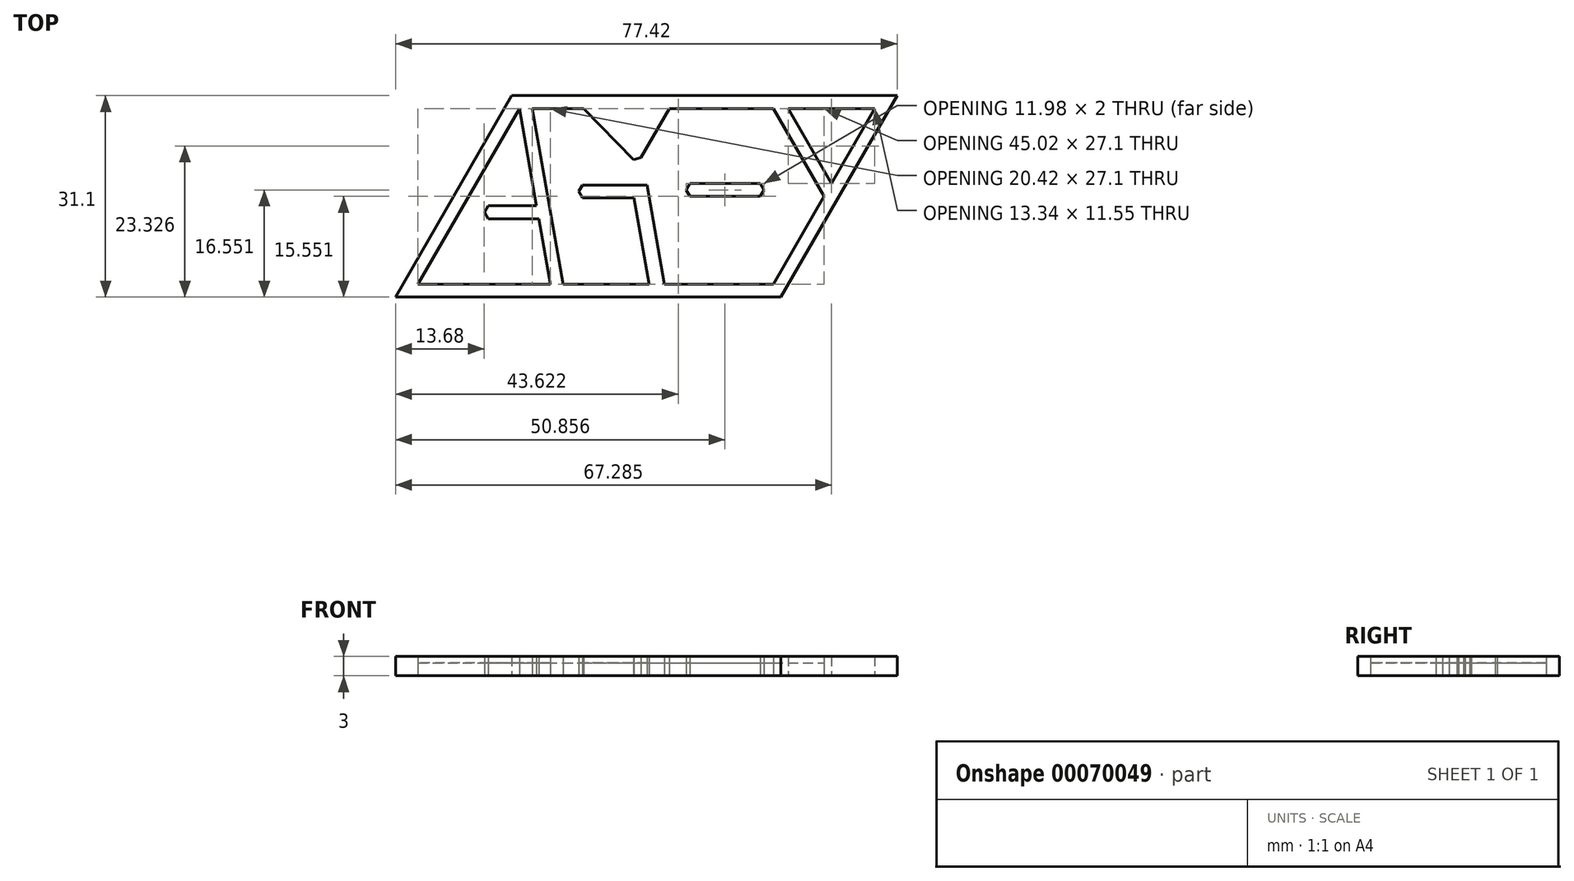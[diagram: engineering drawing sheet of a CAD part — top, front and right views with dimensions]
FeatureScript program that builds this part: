
annotation { "Feature Type Name" : "Feature", "Feature Type Description" : "" }
export const myFeature = defineFeature(function(context is Context, id is Id, definition is map)
    precondition{}
    {
        {
            var Q0;
            Q0=qCreatedBy(makeId("Top.planeOp"),FACE);
            var sketch = newSketch(context, id + "F0", { "sketchPlane" : qUnion([Q0])});
            skLineSegment(sketch, "E0", {"start": v(-33.9, -15.39) * mm, "end": v(-13.47, -15.39) * mm});
            skLineSegment(sketch, "E1", {"start": v(-13.47, -15.39) * mm, "end": v(-18.25, 11.71) * mm});
            skLineSegment(sketch, "E2", {"start": v(-18.25, 11.71) * mm, "end": v(-33.9, -15.39) * mm});
            skLineSegment(sketch, "E3", {"start": v(-15.25, -5.3) * mm, "end": v(-23.05, -5.3) * mm});
            skLineSegment(sketch, "E4", {"start": v(-13.47, -15.39) * mm, "end": v(20.95, -15.39) * mm});
            skLineSegment(sketch, "E5", {"start": v(-18.25, 11.71) * mm, "end": v(20.95, 11.71) * mm});
            skLineSegment(sketch, "E6", {"start": v(20.95, -15.39) * mm, "end": v(28.77, -1.84) * mm});
            skLineSegment(sketch, "E7", {"start": v(28.77, -1.84) * mm, "end": v(20.95, 11.71) * mm});
            skLineSegment(sketch, "E8", {"start": v(18.9, -1.84) * mm, "end": v(8.08, -1.84) * mm});
            skPoint(sketch, "E9.endSnap0", {"position": v(-15.86, -1.84) * mm});
            skLineSegment(sketch, "E10.0", {"start": v(-19.4, 13.71) * mm, "end": v(22.1, 13.71) * mm});
            skLineSegment(sketch, "E10.1", {"start": v(-37.36, -17.39) * mm, "end": v(-13.96, -17.39) * mm});
            skLineSegment(sketch, "E10.2", {"start": v(-13.96, -17.39) * mm, "end": v(22.1, -17.39) * mm});
            skLineSegment(sketch, "E10.3", {"start": v(-19.4, 13.71) * mm, "end": v(-37.36, -17.39) * mm});
            skLineSegment(sketch, "E10.4", {"start": v(22.1, -17.39) * mm, "end": v(31.08, -1.84) * mm});
            skLineSegment(sketch, "E11", {"start": v(-23.05, -3.3) * mm, "end": v(-15.6, -3.3) * mm});
            skLineSegment(sketch, "E12", {"start": v(-16.25, 11.71) * mm, "end": v(-11.47, -15.39) * mm});
            skLineSegment(sketch, "E13", {"start": v(-18.25, 11.71) * mm, "end": v(-16.25, 11.71) * mm});
            skLineSegment(sketch, "E14", {"start": v(1.44, -15.39) * mm, "end": v(-0.56, -15.39) * mm});
            skLineSegment(sketch, "E15", {"start": v(-8.53, -2.08) * mm, "end": v(-0.56, -2.08) * mm});
            skLineSegment(sketch, "E16", {"start": v(8.08, 0.16) * mm, "end": v(18.9, 0.16) * mm});
            skLineSegment(sketch, "E17", {"start": v(1.44, -0.08) * mm, "end": v(-8.53, -0.08) * mm});
            skLineSegment(sketch, "E18", {"start": v(-0.64, 3.83) * mm, "end": v(-8.32, 11.71) * mm});
            skLineSegment(sketch, "E19", {"start": v(-23.05, -5.3) * mm, "end": v(-23.62, -4.3) * mm});
            skLineSegment(sketch, "E20", {"start": v(-23.62, -4.3) * mm, "end": v(-23.05, -3.3) * mm});
            skLineSegment(sketch, "E21", {"start": v(-8.53, -2.08) * mm, "end": v(-9.1, -1.08) * mm});
            skLineSegment(sketch, "E22", {"start": v(-9.1, -1.08) * mm, "end": v(-8.53, -0.08) * mm});
            skLineSegment(sketch, "E23", {"start": v(0.8, 5.23) * mm, "end": v(-5.57, 11.71) * mm});
            skLineSegment(sketch, "E24", {"start": v(-0.64, 3.83) * mm, "end": v(0.48, 4.12) * mm});
            skLineSegment(sketch, "E25", {"start": v(0.48, 4.12) * mm, "end": v(0.8, 5.23) * mm});
            skLineSegment(sketch, "E26", {"start": v(8.08, 0.16) * mm, "end": v(7.5, -0.84) * mm});
            skLineSegment(sketch, "E27", {"start": v(7.5, -0.84) * mm, "end": v(8.08, -1.84) * mm});
            skLineSegment(sketch, "E28", {"start": v(18.9, 0.16) * mm, "end": v(19.49, -0.84) * mm});
            skLineSegment(sketch, "E29", {"start": v(19.49, -0.84) * mm, "end": v(18.9, -1.84) * mm});
            skLineSegment(sketch, "E30", {"start": v(31.08, -1.84) * mm, "end": v(40.06, 13.71) * mm});
            skLineSegment(sketch, "E31", {"start": v(22.1, 13.71) * mm, "end": v(40.06, 13.71) * mm});
            skLineSegment(sketch, "E32", {"start": v(29.93, 0.16) * mm, "end": v(36.6, 11.71) * mm});
            skLineSegment(sketch, "E33", {"start": v(29.93, 0.16) * mm, "end": v(23.26, 11.71) * mm});
            skLineSegment(sketch, "E34", {"start": v(23.26, 11.71) * mm, "end": v(36.6, 11.71) * mm});
            skLineSegment(sketch, "E35", {"start": v(-0.56, -2.08) * mm, "end": v(1.79, -15.39) * mm});
            skLineSegment(sketch, "E36", {"start": v(1.44, -0.08) * mm, "end": v(4.14, -15.39) * mm});
            skLineSegment(sketch, "E37", {"start": v(0.48, 4.12) * mm, "end": v(4.87, 11.71) * mm});
            skLineSegment(sketch, "E38", {"start": v(-19.4, 13.71) * mm, "end": v(-25.03, 16.96) * mm});
            skLineSegment(sketch, "E39", {"start": v(-25.03, 16.96) * mm, "end": v(-42.99, -14.14) * mm});
            skLineSegment(sketch, "E40", {"start": v(-42.99, -14.14) * mm, "end": v(-37.36, -17.39) * mm});
            skLineSegment(sketch, "E41", {"start": v(-25.03, 16.96) * mm, "end": v(41.94, 16.96) * mm});
            skLineSegment(sketch, "E42", {"start": v(41.94, 16.96) * mm, "end": v(40.06, 13.71) * mm});
            skSolve(sketch);
        }
        {
            var Q0;
            {var subQ3=sQuery(id+"F0.wireOp",EDGE,"E0");Q0=makeQuery(id+"F0.imprint","IMPRINT",FACE,{"disambiguationData":[TD([[makeQuery(id+"F0.imprint","IMPRINT",EDGE,{"derivedFrom":subQ3}),1.0]])]});}
            var Q1;
            {var subQ9=sQuery(id+"F0.wireOp",EDGE,"E6");Q1=makeQuery(id+"F0.imprint","IMPRINT",FACE,{"disambiguationData":[TD([[makeQuery(id+"F0.imprint","IMPRINT",EDGE,{"derivedFrom":subQ9}),1.0]])]});}
            extrude(context, id + "F1", {"entities" : qUnion([Q0, Q1]), "depth" : 2 * mm});
        }
        {
            var Q0;
            {var subQ7=sQuery(id+"F0.wireOp",EDGE,"E0");Q0=makeQuery(id+"F0.imprint","IMPRINT",FACE,{"disambiguationData":[TD([[makeQuery(id+"F0.imprint","IMPRINT",EDGE,{"derivedFrom":subQ7}),-1.0]])]});}
            var Q1;
            {var subQ0=sQuery(id+"F0.wireOp",EDGE,"E3");Q1=makeQuery(id+"F0.imprint","IMPRINT",FACE,{"disambiguationData":[TD([[makeQuery(id+"F0.imprint","IMPRINT",EDGE,{"derivedFrom":subQ0}),-1.0]])]});}
            var Q2;
            {var subQ3=sQuery(id+"F0.wireOp",EDGE,"E12");Q2=makeQuery(id+"F0.imprint","IMPRINT",FACE,{"disambiguationData":[TD([[makeQuery(id+"F0.imprint","IMPRINT",EDGE,{"derivedFrom":subQ3}),-1.0]])]});}
            var Q3;
            Q3=makeQuery(id+"F0.imprint","IMPRINT",FACE,{"disambiguationData":[TD([[makeQuery(id+"F0.imprint","IMPRINT",EDGE,{"derivedFrom":sQuery(id+"F0.wireOp",EDGE,"E15")}),1.0]])]});
            var Q4;
            {var subQ0=sQuery(id+"F0.wireOp",EDGE,"E18");Q4=makeQuery(id+"F0.imprint","IMPRINT",FACE,{"disambiguationData":[TD([[makeQuery(id+"F0.imprint","IMPRINT",EDGE,{"derivedFrom":subQ0}),-1.0]])]});}
            var Q5;
            {var subQ0=sQuery(id+"F0.wireOp",EDGE,"E23");Q5=makeQuery(id+"F0.imprint","IMPRINT",FACE,{"disambiguationData":[TD([[makeQuery(id+"F0.imprint","IMPRINT",EDGE,{"derivedFrom":subQ0}),-1.0]])]});}
            var Q6;
            Q6=makeQuery(id+"F0.imprint","IMPRINT",FACE,{"disambiguationData":[TD([[makeQuery(id+"F0.imprint","IMPRINT",EDGE,{"derivedFrom":sQuery(id+"F0.wireOp",EDGE,"E8")}),-1.0]])]});
            extrude(context, id + "F2", {"entities" : qUnion([Q0, Q1, Q2, Q3, Q4, Q5, Q6]), "depth" : 3 * mm});
        }
    });
